# Revit family: result
name_source: partatom
category: Plumbing Fixtures
revit_build: Autodesk Revit 2015 (Build: 20140903_1530(x64)
units: mm (PartAtom-declared; Revit-internal decimal feet)

## types (1)
- Default
    BIMobject category = Bath & Spas
    BIMobject category code = sanitary-bath-spas
    BIMobject main category = Sanitary
    BIMobject main category code = sanitary
    Brand url = https://www.aquaticausa.com
    Edition number = 1
    Installation instructions = https://www.aquaticabath.eu
    Manufacturer name = Aquatica
    Material main = Composite
    Material secondary = Ceramics
    Product Guid = df27415c-7a6c-4db1-b7b8-56bb07d82220
    Product SKU = aquatica-downtown-spa-with-maridur-white-composite-panel
    Product data url = https://bimobject.com
    Product family = Hot tub
    Product group = Spa
    Product name = Aquatica Downtown Spa with Maridur® White Composite Panel
    Product url = https://www.aquaticausa.com
    QR code = http://bimobject.com
    Technical description = https://www.aquaticabath.eu

## geometry (parser evidence)
native form markers: Sweep x3
no freeform markers — native parametric forms only
